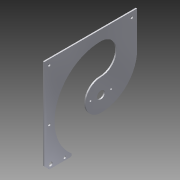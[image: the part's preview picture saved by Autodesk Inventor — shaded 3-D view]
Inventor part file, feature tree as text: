
AUTODESK INVENTOR PART (.ipt)
format: ipt  version: 2015 (Build 190159000, 159)  size: 217,088 bytes
history: native  units: in
note: dims shown in document units (in); Inventor stores cm internally (conversion verified against a paired STEP export)
features: sketch x6, projected_geometry x5, extrude x4, hole x2, fillet x1
ambient origin geometry x8: Origin, YZ Plane, XZ Plane, XY Plane, X Axis, Y Axis, Z Axis, Center Point
bodies: Solid1 (feature_tree)
feature tree (18):
  extrude  "Extrusion1"  Depth=2.5in
  extrude  "Extrusion2"  Depth=3.25in
  hole  "Hole1"  [1 undecoded]
  extrude  "Extrusion3"  Depth=9.0in
  extrude  "Extrusion4"  Depth=3.0in
  hole  "Hole3"  [1 undecoded]
  fillet  "Fillet1"  Radius=5.5in
  sketch  "Sketch1"  dims[d0=4.0in d1=2.5in]
  sketch  "Sketch2"  dims[d2=2.5in d3=3.25in]
  projected_geometry  "Projected Loop1"
  sketch  "Sketch3"  dims[d4=3.25in d5=0.0in]
  projected_geometry  "Projected Loop2"
  sketch  "Sketch4"  dims[d6=0.0in d7=9.0in]
  projected_geometry  "Projected Loop3"
  sketch  "Sketch5"  dims[d8=3.0in d9=3.0in]
  projected_geometry  "Projected Loop4"
  sketch  "Sketch6"  dims[d10=7.0in d11=3.5in d12=5.5in d13=0.0in d14=9.5in d15=5.5in d16=0.0in d22=0.125in d23=0.0in d24=3.0in d25=0.25in d26=0.5in d27=0.125in d28=0.0in d29=0.5in d30=0.5in d31=0.5in d32=0.5in d33=0.5in d34=5.5in d35=3.75in d36=3.25in d37=0.25in d38=0.75in d39=0.375in d40=0.25in d41=0.5635in d42=1.0in d43=0.8108in d44=0.0in d45=0.0in d46=1.0in d47=1.0in d55=0.75in d56=0.1875in d57=0.1875in d58=0.125in d59=0.0in d60=0.5in d61=0.5in d62=0.125in d63=0.0in d64=0.625in d65=0.375in d66=0.375in d67=0.75in d68=0.375in d69=0.25in d70=0.5635in d71=1.0in d72=0.8108in d73=0.125in d74=0.25in d75=1.7in]
  projected_geometry  "Projected Loop5"
note: 2 required parameter values undecoded (feature->parameter linkage not recoverable at this tier; creation-order binding heuristic only, values carry confidence <= 0.55)
